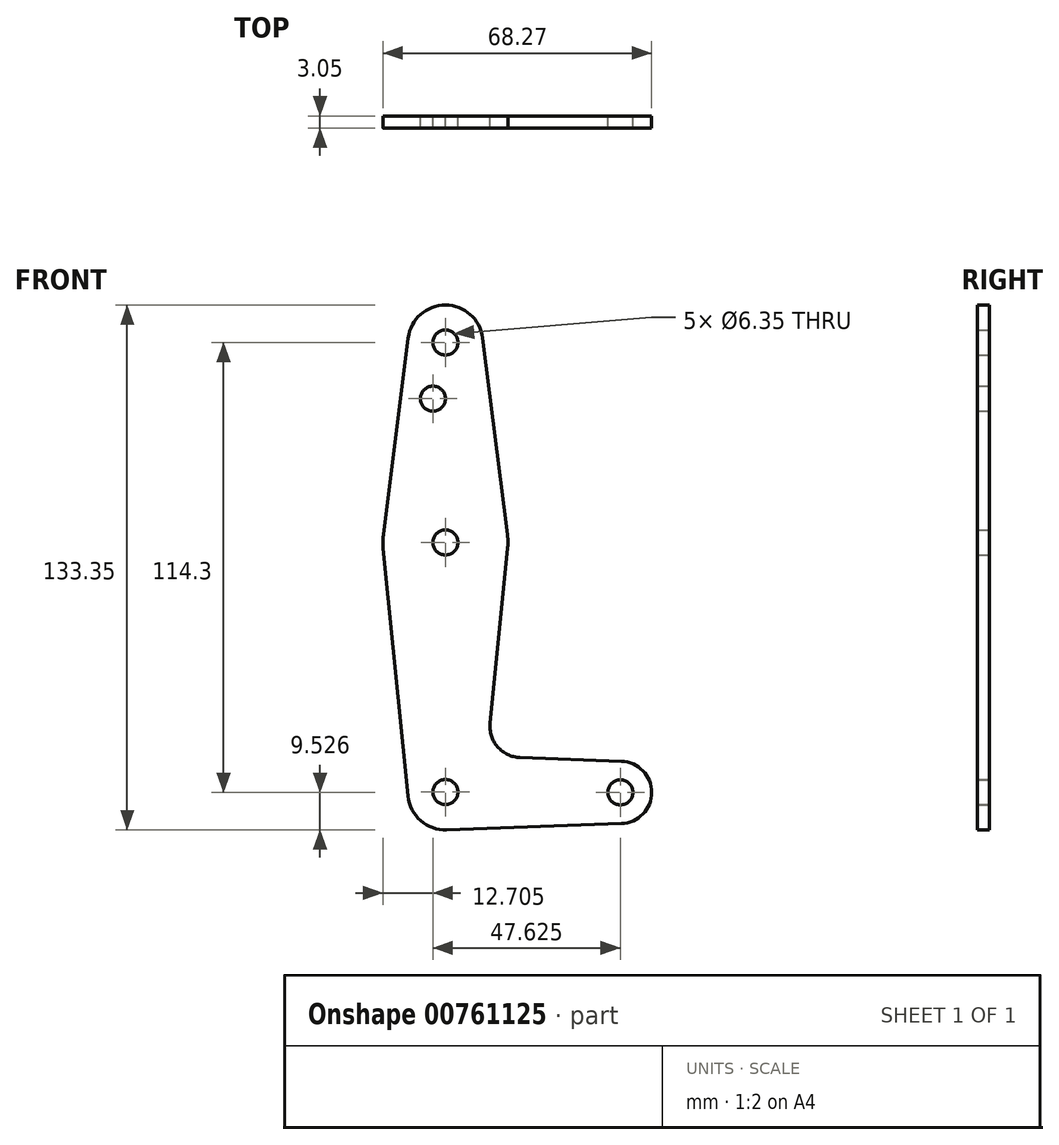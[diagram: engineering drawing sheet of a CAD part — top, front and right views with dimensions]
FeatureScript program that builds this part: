
annotation { "Feature Type Name" : "Feature", "Feature Type Description" : "" }
export const myFeature = defineFeature(function(context is Context, id is Id, definition is map)
    precondition{}
    {
        {
            var Q0;
            Q0=qCreatedBy(makeId("Front.planeOp"),FACE);
            var sketch = newSketch(context, id + "F0", { "sketchPlane" : qUnion([Q0])});
            skLineSegment(sketch, "E0", {"start": v(0, 114.23) * mm, "end": v(0, -0.07) * mm, "construction": true});
            skLineSegment(sketch, "E1", {"start": v(0, -0.07) * mm, "end": v(44.45, -0.07) * mm, "construction": true});
            skCircle(sketch, "E2", {"center": v(0, 114.23) * mm, "radius": 9.53 * mm});
            skCircle(sketch, "E3", {"center": v(0, 63.43) * mm, "radius": 15.88 * mm});
            skCircle(sketch, "E4", {"center": v(0, -0.07) * mm, "radius": 9.53 * mm});
            skCircle(sketch, "E5", {"center": v(44.45, -0.07) * mm, "radius": 7.94 * mm});
            skLineSegment(sketch, "E6", {"start": v(-9.45, 115.42) * mm, "end": v(-15.75, 65.41) * mm});
            skLineSegment(sketch, "E7", {"start": v(-15.8, 61.84) * mm, "end": v(-9.48, -1.03) * mm});
            skLineSegment(sketch, "E8", {"start": v(9.45, 115.42) * mm, "end": v(15.75, 65.41) * mm});
            skLineSegment(sketch, "E9", {"start": v(15.8, 61.84) * mm, "end": v(11.34, 17.52) * mm});
            skLineSegment(sketch, "E10", {"start": v(18.97, 8.78) * mm, "end": v(44.73, 7.86) * mm});
            skLineSegment(sketch, "E11", {"start": v(0.34, -9.6) * mm, "end": v(44.73, -8) * mm});
            skCircle(sketch, "E12", {"center": v(0, 114.23) * mm, "radius": 3.18 * mm});
            skCircle(sketch, "E13", {"center": v(0, 63.43) * mm, "radius": 3.18 * mm});
            skCircle(sketch, "E14", {"center": v(0, 0) * mm, "radius": 3.18 * mm});
            skCircle(sketch, "E15", {"center": v(44.45, -0.07) * mm, "radius": 3.18 * mm});
            skCircle(sketch, "E16", {"center": v(-3.17, 99.95) * mm, "radius": 3.18 * mm});
            skArc(sketch, "E17.filletArc", {"start": v(11.34, 17.52) * mm, "mid": v(13.26, 11.5) * mm, "end": v(18.97, 8.78) * mm});
            skSolve(sketch);
        }
        {
            var Q0;
            Q0 = qSketchRegion(id + "F0", true);
            extrude(context, id + "F1", {"entities" : qUnion([Q0]), "depth" : 3.05 * mm, "offsetDistance" : 25.4 * mm});
        }
    });
